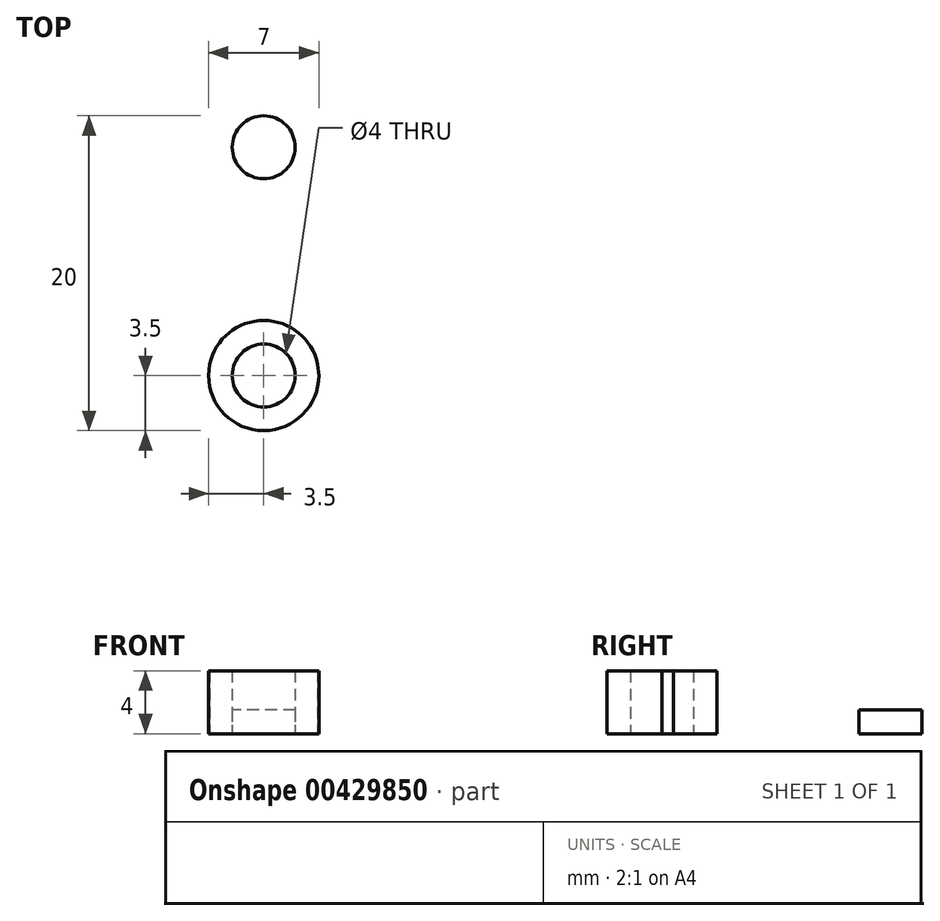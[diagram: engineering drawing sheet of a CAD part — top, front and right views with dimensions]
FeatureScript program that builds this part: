
annotation { "Feature Type Name" : "Feature", "Feature Type Description" : "" }
export const myFeature = defineFeature(function(context is Context, id is Id, definition is map)
    precondition{}
    {
        {
            var Q0;
            Q0=qCreatedBy(makeId("Top.planeOp"),FACE);
            var sketch = newSketch(context, id + "F0", { "sketchPlane" : qUnion([Q0])});
            skCircle(sketch, "E0", {"center": v(0, 0) * mm, "radius": 3.5 * mm});
            skCircle(sketch, "E1", {"center": v(0, 0) * mm, "radius": 2 * mm});
            skLineSegment(sketch, "E2", {"start": v(0, 0) * mm, "end": v(0, 14.5) * mm, "construction": true});
            skCircle(sketch, "E3", {"center": v(0, 14.5) * mm, "radius": 2 * mm});
            skLineSegment(sketch, "E4", {"start": v(-3.5, 0) * mm, "end": v(-2, 14.5) * mm});
            skLineSegment(sketch, "E5", {"start": v(3.5, 0) * mm, "end": v(2, 14.5) * mm});
            skSolve(sketch);
        }
        {
            var Q0;
            {var subQ0=sQuery(id+"F0.wireOp",EDGE,"E3");var subQ1=makeQuery(id+"F0.imprint","INTERSECT",VERTEX,{"derivedFrom":[subQ0,sQuery(id+"F0.wireOp",EDGE,"E4")]});Q0=makeQuery(id+"F0.imprint","IMPRINT",FACE,{"disambiguationData":[TD([[makeQuery(id+"F0.imprint","IMPRINT",EDGE,{"disambiguationData":[TD([[subQ1,1.0]])],"derivedFrom":subQ0}),1.0]])]});}
            var Q1;
            {var subQ0=sQuery(id+"F0.wireOp",EDGE,"E5");var subQ1=sQuery(id+"F0.wireOp",EDGE,"E0");var subQ2=makeQuery(id+"F0.imprint","INTERSECT",VERTEX,{"disambiguationData":[OD(1.0)],"derivedFrom":[subQ1,subQ0]});Q1=makeQuery(id+"F0.imprint","IMPRINT",FACE,{"disambiguationData":[TD([[makeQuery(id+"F0.imprint","IMPRINT",EDGE,{"disambiguationData":[TD([[subQ2,-1.0]])],"derivedFrom":subQ1}),-1.0]])]});}
            extrude(context, id + "F1", {"entities" : qUnion([Q0, Q1]), "depth" : 1.5 * mm, "offsetDistance" : 25 * mm});
        }
        {
            var Q0;
            Q0=makeQuery(id+"F0.imprint","IMPRINT",FACE,{"disambiguationData":[TD([[makeQuery(id+"F0.imprint","IMPRINT",EDGE,{"derivedFrom":sQuery(id+"F0.wireOp",EDGE,"E1")}),-1.0]])]});
            extrude(context, id + "F2", {"entities" : qUnion([Q0]), "operationType" : NewBodyOperationType.ADD, "depth" : 4 * mm, "offsetDistance" : 25 * mm});
        }
    });
